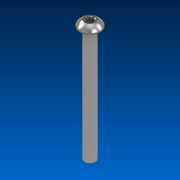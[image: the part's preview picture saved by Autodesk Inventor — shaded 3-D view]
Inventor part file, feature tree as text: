
AUTODESK INVENTOR PART (.ipt)
format: ipt  version: 2022.2 (Build 262287000, 287)  size: 168,960 bytes
history: native  units: in
note: dims shown in document units (in); Inventor stores cm internally (conversion verified against a paired STEP export)
features: direct_edit x1, chamfer x1, move_body x1
ambient origin geometry x8: Origin, YZ Plane, XZ Plane, XY Plane, X Axis, Y Axis, Z Axis, Center Point
bodies: Solid1 (feature_tree)
feature tree (3):
  direct_edit  "Direct Edit1"
  chamfer  "Chamfer2"  [1 undecoded]
  move_body  "Move1"
note: 1 required parameter value undecoded (feature->parameter linkage not recoverable at this tier; creation-order binding heuristic only, values carry confidence <= 0.55)
